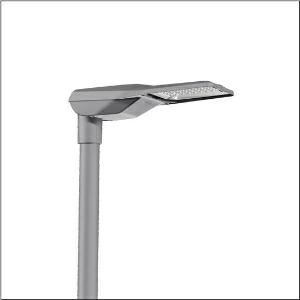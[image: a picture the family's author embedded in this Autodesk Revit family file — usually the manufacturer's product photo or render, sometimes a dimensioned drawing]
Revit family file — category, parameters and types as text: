
# Revit family: streetlight_sl_21_iq_mini___st1_0a_5xe2d41g08jb_4fff
name_source: partatom
category: Lighting Fixtures
units: mm (PartAtom-declared; Revit-internal decimal feet)

## family parameters
Cut with Voids When Loaded = No
Host = Face
Light Source = No
Part Type = Normal
Room Calculation Point = No
Round Connector Dimension = Use Diameter
Shared = No

## types (1)
- --- (1 x LED, 11290 lm, 71.6 W, 4000K)
    Apparent Load = 72 VA
    CIE Flux Codes = 40 73 97 100 100
    Color Rendering = 70
    Color Temperature = 4000K
    Default Elevation = 1800 mm
    Description = Streetlight SL 21 iQ mini, mast luminaire, primary light control with lens, of PMMA, primary optical cover: cover, of toughened safety glass, transparent, light distribution: ST1.0a, light emission: direct distribution, primary light characteristic: asymmetric, installation type: post-top, side-entry, LED, High Power LED, rated luminous flux: 11.290lm, luminous efficacy: 158lm/W, light colour: 740, colour temperature: 4000K, control: Street-Remote, Auto-Match, Temp-Guard, Lumen-Switch, Night-Set, Smart-Wire, Light-Fading, Desk-Remote (wireless, voltage-free reading and setting of iQ features in the workshop via application-optimized NFC function/RFID function), optimised constant luminous flux control (CLO 2.0), presetting dimming linear, mains connection: 220..240V, AC, 50/60Hz, start of lifetime: 72W, end of service life: 75W, reduction: 33W, luminaire housing, of diecast aluminium, powder-coated, Siteco® metallic grey (DB 702S), corrosivity category C5 mid according to DIN EN ISO 12944, please order mast flange separately, inclination adjustable: 0°, 5°, 10°, 15°, sealing non-destructively replaceable, multi-level sealing system, length: 628mm, width: 235mm, height: 110mm, mast flange for spigot size: 42mm (side-entry): 5XC10008XM4, 60/48mm (side-entry/post-top): 5XC10108XM2, 76/60mm (side-entry/post-top): 5XC10108XM1, protection rating (complete): IP66, insulation class (complete): insulation class II (safety insulation), certification: CE, ENEC, ENEC+, VDE, impact resistance: IK09, permissible operating ambient temperature for outdoor applications: -40..+50°C, standard-compliant lighting for roads and squares, packaging unit: 1 piece

Light Distribution: ST1.0a
    Height = 110 mm
    Lamp = 1 x LED
    Lamp Light Flux = 11290 lm
    Lamp Power = 71.6 W
    Lamp count = 1
    Length = 625 mm
    Luminous efficacy = 158 lm/W
    Manufacturer = Siteco
    ModVariant = No
    Model = 5XE2D41G08JB
    Number of Poles = 1
    OnlyDefault = Yes
    Power Factor = 1
    Product Name = Streetlight SL 21 iQ mini | ST1.0a
    Product group = mast luminaire | pylon top
    ProductGroupID = 6100
    Protection Class = Protection class II
    Protection Degree = IP 66
    RLX_Detail_Level = 1
    RLX_Emergency_Light_Flux = 0 lm
    RLX_Emergency_Type = 0
    RLX_Emergency_Type_DB = No
    RlxData = <blob elided: 91969 chars, md5=9e4997ef>
    Socket = socket
    Standby Power = 0 W
    System Light Flux = 11290 lm
    System Power = 72 W
    Type Comments = factory setting: luminous flux: 100 % | dim-lin: 254 | 746 mA
    Type Image = l_1003519.jpg
    URL = http://relux.com
    VarID = @adj_121861
    Voltage = 0 V
    Weight = 0.00 kg
    Width = 234 mm

## geometry (parser evidence)
native form markers: Blend x4, Sweep x11
no freeform markers — native parametric forms only
